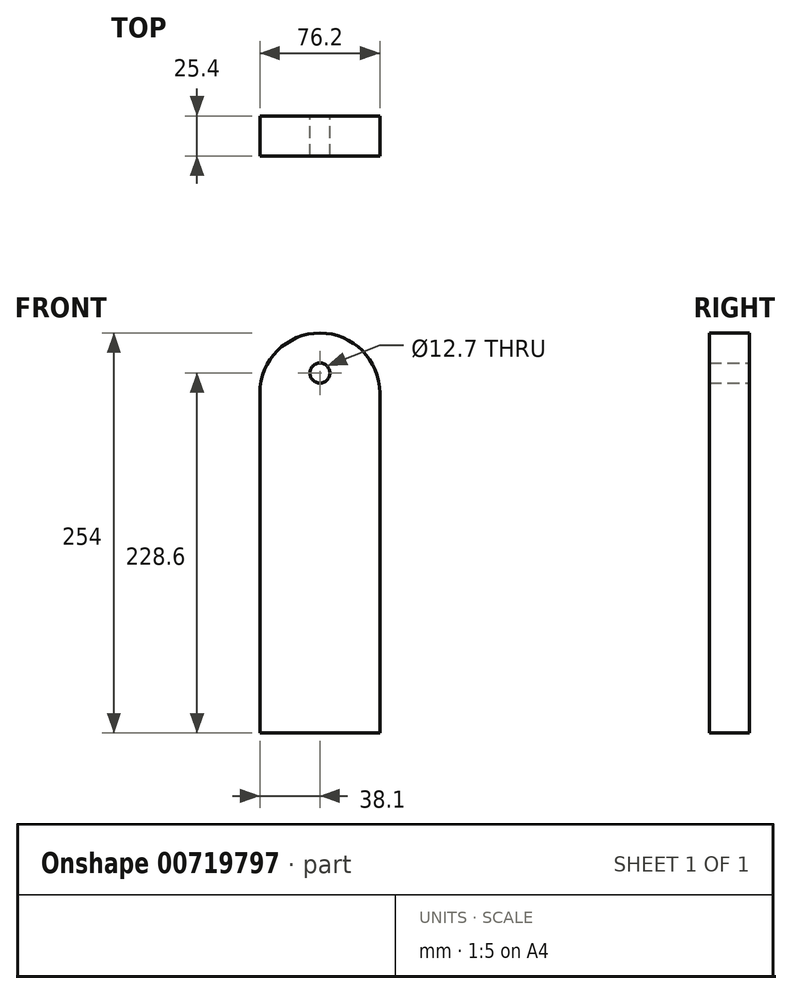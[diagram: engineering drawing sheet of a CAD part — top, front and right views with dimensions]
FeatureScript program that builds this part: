
annotation { "Feature Type Name" : "Feature", "Feature Type Description" : "" }
export const myFeature = defineFeature(function(context is Context, id is Id, definition is map)
    precondition{}
    {
        {
            var Q0;
            Q0=qCreatedBy(makeId("Front.planeOp"),FACE);
            var sketch = newSketch(context, id + "F0", { "sketchPlane" : qUnion([Q0])});
            skLineSegment(sketch, "E0.bottom", {"start": v(-76.2, 254) * mm, "end": v(0, 254) * mm});
            skLineSegment(sketch, "E0.top", {"start": v(-76.2, 0) * mm, "end": v(0, 0) * mm});
            skLineSegment(sketch, "E0.left", {"start": v(-76.2, 254) * mm, "end": v(-76.2, 0) * mm});
            skLineSegment(sketch, "E0.right", {"start": v(0, 254) * mm, "end": v(0, 0) * mm});
            skCircle(sketch, "E1", {"center": v(-38.1, 228.6) * mm, "radius": 6.35 * mm});
            skSolve(sketch);
        }
        {
            var Q0;
            Q0=makeQuery(id+"F0.imprint","IMPRINT",FACE,{"disambiguationData":[TD([[makeQuery(id+"F0.imprint","IMPRINT",EDGE,{"derivedFrom":sQuery(id+"F0.wireOp",EDGE,"E0.bottom")}),1.0]])]});
            var Q1;
            Q1=makeQuery(id+"F0.imprint","IMPRINT",FACE,{"disambiguationData":[TD([[makeQuery(id+"F0.imprint","IMPRINT",EDGE,{"derivedFrom":sQuery(id+"F0.wireOp",EDGE,"E0.bottom")}),-1.0]])]});
            extrude(context, id + "F1", {"entities" : qUnion([Q0, Q1]), "depth" : 25.4 * mm, "offsetDistance" : 25.4 * mm});
        }
        {
            var Q0;
            Q0=makeQuery(id+"F1.opExtrude","SWEPT_EDGE",EDGE,{"disambiguationData":[OSD([sQuery(id+"F0.wireOp",EDGE,"E0.bottom"),sQuery(id+"F0.wireOp",EDGE,"E0.left")])]});
            var Q1;
            Q1=makeQuery(id+"F1.opExtrude","SWEPT_EDGE",EDGE,{"disambiguationData":[OSD([sQuery(id+"F0.wireOp",EDGE,"E0.bottom"),sQuery(id+"F0.wireOp",EDGE,"E0.right")])]});
            fillet(context, id + "F2", {"entities" : qUnion([Q0, Q1]), "radius" : 38.1 * mm, "tangentPropagation" : true, "allowEdgeOverflow" : false});
        }
    });
